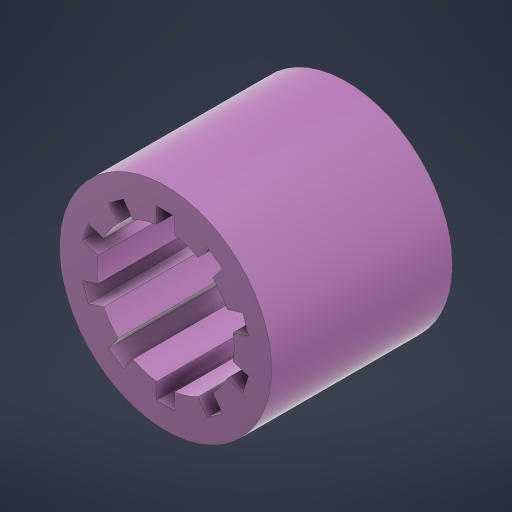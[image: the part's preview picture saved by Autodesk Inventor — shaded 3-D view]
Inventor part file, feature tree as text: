
AUTODESK INVENTOR PART (.ipt)
format: ipt  version: 2024 (Build 280153000, 153)  size: 273,920 bytes
history: native  units: in
note: dims shown in document units (in); Inventor stores cm internally (conversion verified against a paired STEP export)
features: extrude x1, sketch x1
ambient origin geometry x8: Origin, YZ Plane, XZ Plane, XY Plane, X Axis, Y Axis, Z Axis, Center Point
bodies: Solid1 (feature_tree)
feature tree (2):
  extrude  "Extrusion1"  Depth=0.1138in
  sketch  "Sketch1"  dims[d1=3.937in d2=360.0deg d3=1.3386in d4=1.1417in d5=0.0in d6=0.4331in d7=0.6693in d8=0.1021in d9=0.1138in]
